# Revit family: Faucet-Kitchen-KALLISTA-Pre_Se-P24735
name_source: partatom
category: Plumbing Fixtures
units: mm (PartAtom-declared; Revit-internal decimal feet)

## family parameters
Cut with Voids When Loaded = No
Host = Face
Maintain Annotation Orientation = No
OmniClass Number = 23.31.11.00
OmniClass Title = Faucets
Part Type = Normal
Room Calculation Point = No
Round Connector Dimension = Use Diameter
Shared = No

## types (4) — shared parameters
ADA Compliant = No
Assembly Code = D2010
CW Connection = Yes
Cold Water Inlet = Cold Water Inlet
Date Modified = 09/30/2025
Default Elevation = 36"
Description = Bidet Faucet Set
Drain Included = Yes
Flow Rate = 0 GPM
HW Connection = Yes
Handle Clearance = 3 1/16"
Height = 5 3/8"
Hot Water Inlet = Hot Water Inlet
Length = 2 1/4"
Manufacturer = Kallista Co.
Master Format 2014 = 22 41 39
Master Format 2014 Name = Residential Faucets, Supplies, and Trim
Material = Premium Metal Construction
Pressure = 0.00 psi
Product Name = Pre Se
URL = https://www.kallista.com
Vent Connection = No
Waste Connection = No
Waste Water Outlet = Waste Water Outlet
WaterSense Certified = No

## per-type parameters (varying)
| type | Finish | Model | Type |
| AD-Nickel Silver | Kallista-Metal-AD-Nickel_Silver | P24735-LV-AD | 1 |
| AF-French Gold | Kallista-Metal-AF-French_Gold | P24735-LV-AF | 2 |
| AG-Brushed Nickel | Kallista-Metal-AG-Brushed_Nickel | P24735-LV-AG | 3 |
| CP-Chrome | Kallista-Metal-CP-Chrome | P24735-LV-CP | 4 |

## geometry (parser evidence)
native form markers: Sweep x10
no freeform markers — native parametric forms only
